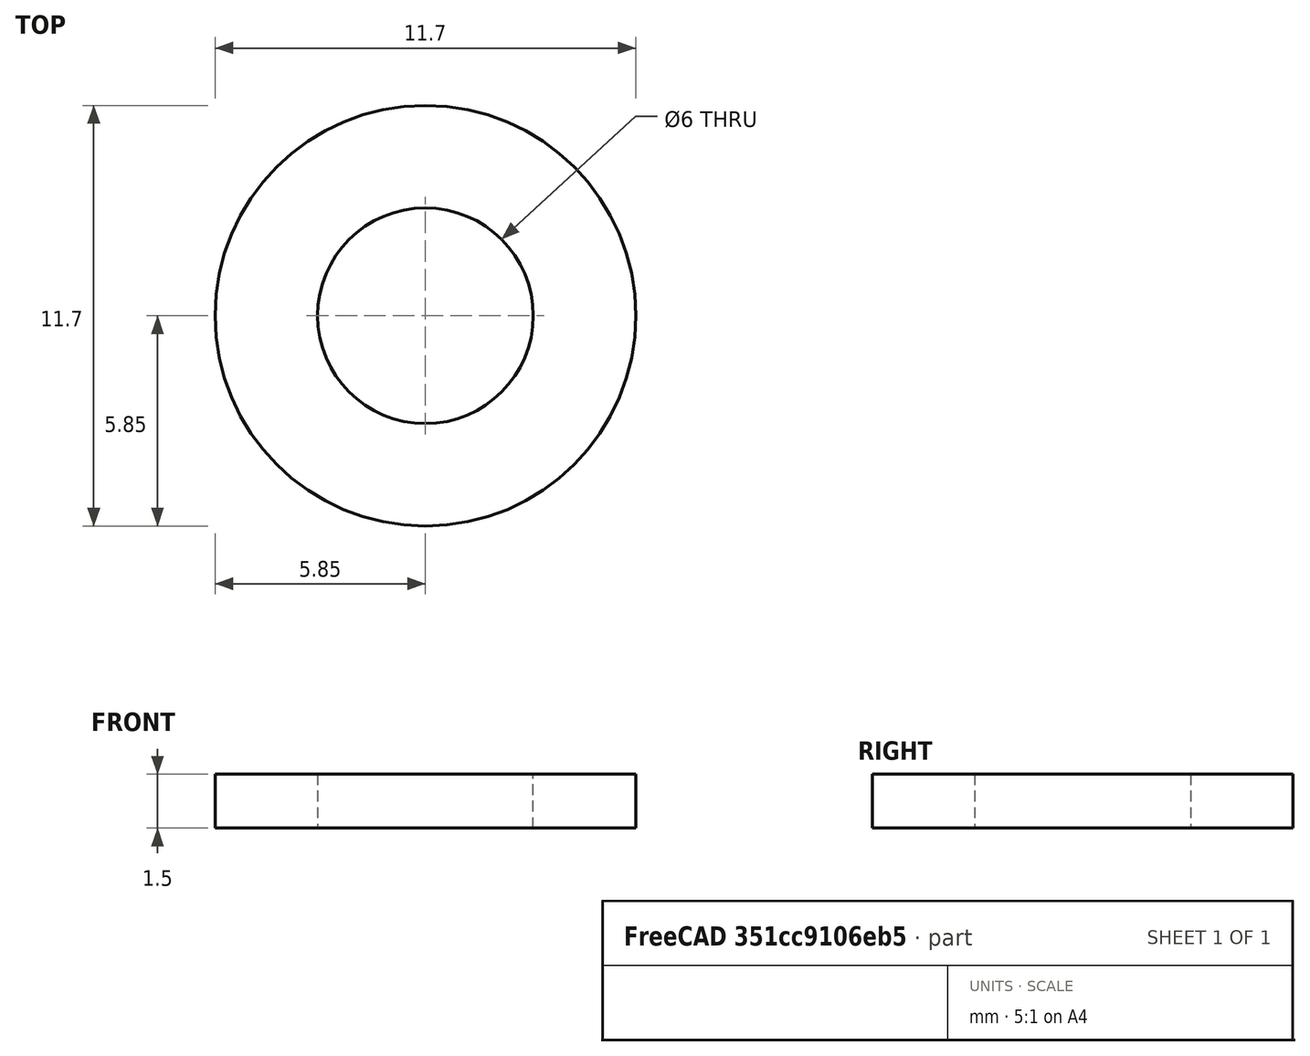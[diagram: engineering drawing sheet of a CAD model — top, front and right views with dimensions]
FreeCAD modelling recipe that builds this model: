
FCSTD DOCUMENT  (FreeCAD 0.18.4R)
Label: M6_Washer
License: All rights reserved
LicenseURL: http://en.wikipedia.org/wiki/All_rights_reserved
objects: Sketcher::SketchObject×1, PartDesign::Pad×1, PartDesign::Body×1
note: 4 computed .brp shape members not serialized (recipe doc carries the construction recipe); baked Part::Feature solids carry a one-line shape summary decoded from their .brp

FEATURE [Sketcher::SketchObject] Sketch
  MapMode = 5
  Support = -> [XY_Plane]
  sketch-geometry (2):
    g0: Circle CenterX=0 CenterY=0 CenterZ=0 NormalX=0 NormalY=0 NormalZ=1 AngleXU=0 Radius=5.85
    g1: Circle CenterX=0 CenterY=0 CenterZ=0 NormalX=0 NormalY=0 NormalZ=1 AngleXU=0 Radius=3
  constraints (4):
    c: Coincident(g1,g0)
    c: Coincident(g1,g-1)
    c: Diameter(g1) = 6
    c: Diameter(g0) = 11.7
FEATURE [PartDesign::Pad] Pad
  Length = 1.5
  Length2 = 100
  Profile = -> Sketch
  Type = 0
FEATURE [PartDesign::Body] Body  label="M6_Washer"
  Group = -> [Sketch,Pad]
  Origin = -> Origin
  Tip = -> Pad
